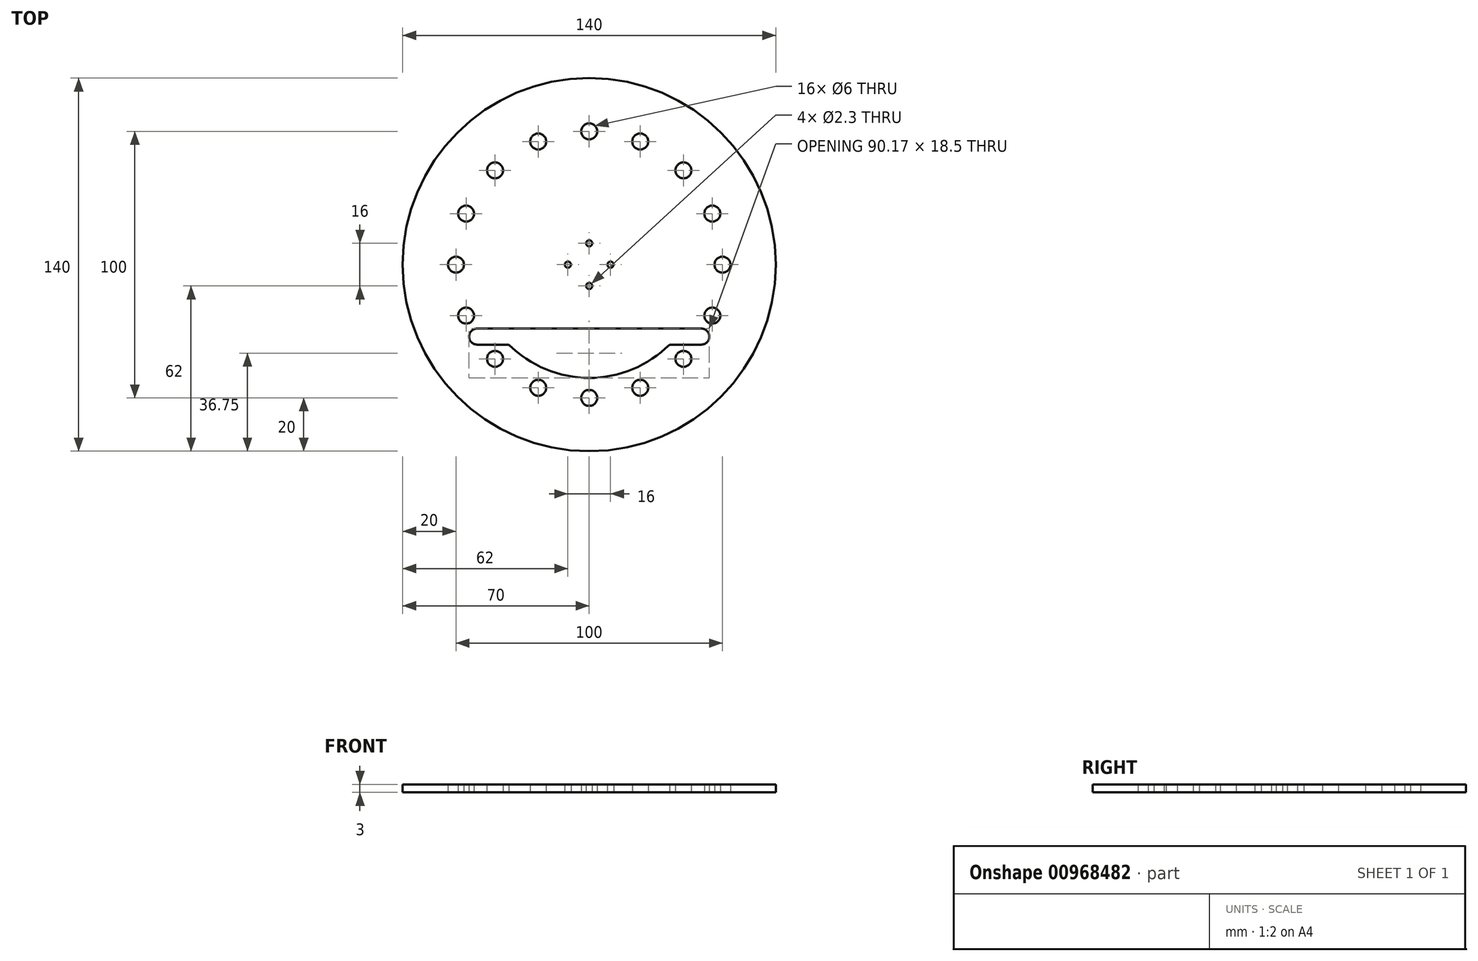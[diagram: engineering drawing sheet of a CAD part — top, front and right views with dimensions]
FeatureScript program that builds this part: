
annotation { "Feature Type Name" : "Feature", "Feature Type Description" : "" }
export const myFeature = defineFeature(function(context is Context, id is Id, definition is map)
    precondition{}
    {
        {
            var Q0;
            Q0=qCreatedBy(makeId("Top.planeOp"),FACE);
            var sketch = newSketch(context, id + "F0", { "sketchPlane" : qUnion([Q0])});
            skCircle(sketch, "E0", {"center": v(0, 0) * mm, "radius": 70 * mm});
            skCircle(sketch, "E1", {"center": v(0, 0) * mm, "radius": 50 * mm, "construction": true});
            skCircle(sketch, "E2", {"center": v(0, 50) * mm, "radius": 3 * mm});
            skCircle(sketch, "E3.1.0", {"center": v(-19.13, 46.2) * mm, "radius": 3 * mm});
            skCircle(sketch, "E3.2.0", {"center": v(-35.36, 35.36) * mm, "radius": 3 * mm});
            skCircle(sketch, "E3.3.0", {"center": v(-46.2, 19.13) * mm, "radius": 3 * mm});
            skCircle(sketch, "E3.4.0", {"center": v(-50, 0) * mm, "radius": 3 * mm});
            skCircle(sketch, "E3.5.0", {"center": v(-46.2, -19.13) * mm, "radius": 3 * mm});
            skCircle(sketch, "E3.6.0", {"center": v(-35.36, -35.36) * mm, "radius": 3 * mm});
            skCircle(sketch, "E3.7.0", {"center": v(-19.13, -46.2) * mm, "radius": 3 * mm});
            skCircle(sketch, "E3.8.0", {"center": v(0, -50) * mm, "radius": 3 * mm});
            skCircle(sketch, "E3.9.0", {"center": v(19.13, -46.2) * mm, "radius": 3 * mm});
            skCircle(sketch, "E3.10.0", {"center": v(35.36, -35.36) * mm, "radius": 3 * mm});
            skCircle(sketch, "E3.11.0", {"center": v(46.2, -19.13) * mm, "radius": 3 * mm});
            skCircle(sketch, "E3.12.0", {"center": v(50, 0) * mm, "radius": 3 * mm});
            skCircle(sketch, "E3.13.0", {"center": v(46.2, 19.13) * mm, "radius": 3 * mm});
            skCircle(sketch, "E3.14.0", {"center": v(35.36, 35.36) * mm, "radius": 3 * mm});
            skCircle(sketch, "E3.15.0", {"center": v(19.13, 46.2) * mm, "radius": 3 * mm});
            skArc(sketch, "E4", {"start": v(-30.1, -30) * mm, "mid": v(0, -42.5) * mm, "end": v(30.1, -30) * mm});
            skArc(sketch, "E5", {"start": v(-42.08, -24) * mm, "mid": v(-45.08, -27) * mm, "end": v(-42.08, -30) * mm});
            skArc(sketch, "E6", {"start": v(42.08, -30) * mm, "mid": v(45.08, -27) * mm, "end": v(42.08, -24) * mm});
            skLineSegment(sketch, "E7", {"start": v(-42.08, -24) * mm, "end": v(-35.07, -24) * mm});
            skLineSegment(sketch, "E8", {"start": v(-42.08, -30) * mm, "end": v(-30.1, -30) * mm});
            skLineSegment(sketch, "E9.trimOffspring", {"start": v(35.07, -24) * mm, "end": v(42.08, -24) * mm});
            skLineSegment(sketch, "E10.trimOffspring", {"start": v(30.1, -30) * mm, "end": v(42.08, -30) * mm});
            skLineSegment(sketch, "E11", {"start": v(-35.07, -24) * mm, "end": v(35.07, -24) * mm});
            skCircle(sketch, "E12", {"center": v(0, 0) * mm, "radius": 8 * mm, "construction": true});
            skCircle(sketch, "E13", {"center": v(0, 8) * mm, "radius": 1.15 * mm});
            skCircle(sketch, "E14.1.1", {"center": v(-8, 0) * mm, "radius": 1.15 * mm});
            skCircle(sketch, "E14.2.1", {"center": v(0, -8) * mm, "radius": 1.15 * mm});
            skCircle(sketch, "E14.3.1", {"center": v(8, 0) * mm, "radius": 1.15 * mm});
            skSolve(sketch);
        }
        {
            var Q0;
            Q0=qSketchRegion(id+"F0",true);
            extrude(context, id + "F1", {"entities" : qUnion([Q0]), "depth" : 3 * mm, "offsetDistance" : 25 * mm});
        }
    });
